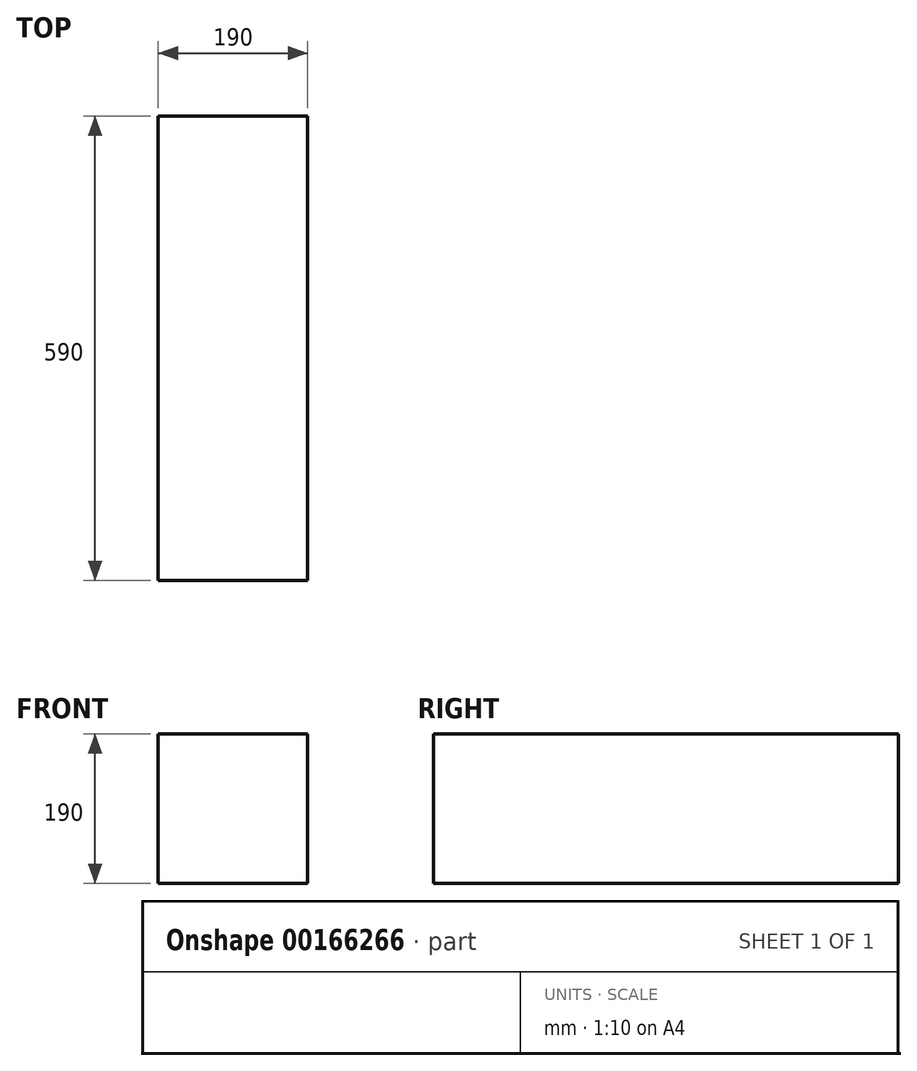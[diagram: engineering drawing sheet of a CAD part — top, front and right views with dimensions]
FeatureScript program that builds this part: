
annotation { "Feature Type Name" : "Feature", "Feature Type Description" : "" }
export const myFeature = defineFeature(function(context is Context, id is Id, definition is map)
    precondition{}
    {
        {
            var Q0;
            Q0=qCreatedBy(makeId("Front.planeOp"),FACE);
            var sketch = newSketch(context, id + "F0", { "sketchPlane" : qUnion([Q0])});
            skLineSegment(sketch, "E0.bottom", {"start": v(0, 0) * mm, "end": v(190, 0) * mm});
            skLineSegment(sketch, "E0.top", {"start": v(0, 190) * mm, "end": v(190, 190) * mm});
            skLineSegment(sketch, "E0.left", {"start": v(0, 0) * mm, "end": v(0, 190) * mm});
            skLineSegment(sketch, "E0.right", {"start": v(190, 0) * mm, "end": v(190, 190) * mm});
            skSolve(sketch);
        }
        {
            var Q0;
            Q0 = qSketchRegion(id + "F0", true);
            extrude(context, id + "F1", {"entities" : qUnion([Q0]), "depth" : 590 * mm});
        }
    });
